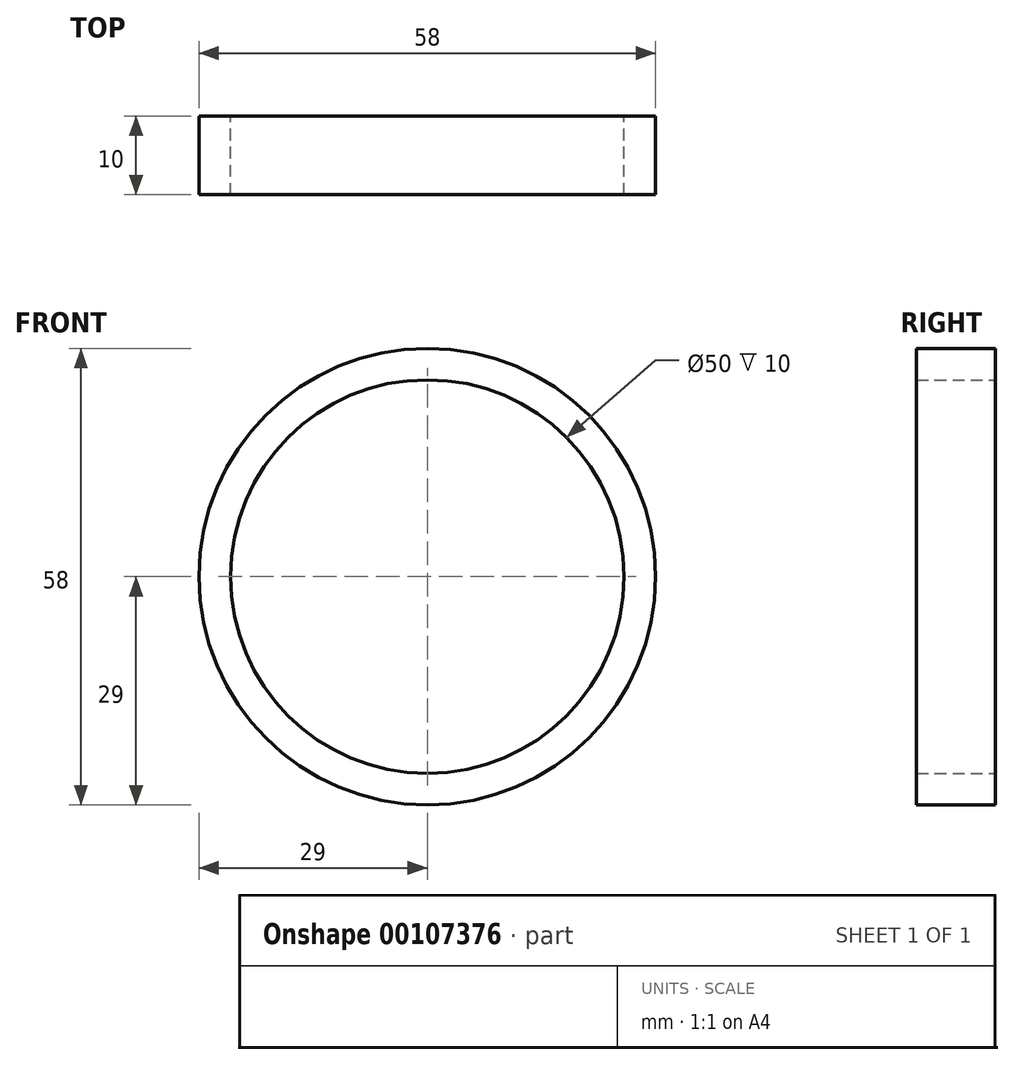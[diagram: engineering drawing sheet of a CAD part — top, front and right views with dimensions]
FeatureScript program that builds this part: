
annotation { "Feature Type Name" : "Feature", "Feature Type Description" : "" }
export const myFeature = defineFeature(function(context is Context, id is Id, definition is map)
    precondition{}
    {
        {
            var Q0;
            Q0=qCreatedBy(makeId("Front.planeOp"),FACE);
            var sketch = newSketch(context, id + "F0", { "sketchPlane" : qUnion([Q0])});
            skCircle(sketch, "E0", {"center": v(0, 0) * mm, "radius": 29 * mm});
            skSolve(sketch);
        }
        {
            var Q0;
            Q0=makeQuery(id+"F0.imprint","IMPRINT",FACE,{"disambiguationData":[TD([[makeQuery(id+"F0.imprint","IMPRINT",EDGE,{"derivedFrom":sQuery(id+"F0.wireOp",EDGE,"E0")}),1.0]])]});
            var sketch = newSketch(context, id + "F1", { "sketchPlane" : qUnion([Q0])});
            skCircle(sketch, "E1", {"center": v(0, 0) * mm, "radius": 25 * mm});
            skSolve(sketch);
        }
        {
            var Q0;
            Q0=makeQuery(id+"F0.imprint","IMPRINT",FACE,{"disambiguationData":[TD([[makeQuery(id+"F0.imprint","IMPRINT",EDGE,{"derivedFrom":sQuery(id+"F0.wireOp",EDGE,"E0")}),1.0]])]});
            extrude(context, id + "F2", {"entities" : qUnion([Q0]), "depth" : 10 * mm});
        }
        {
            var Q0;
            Q0=makeQuery(id+"F1.imprint","IMPRINT",FACE,{"disambiguationData":[TD([[makeQuery(id+"F1.imprint","IMPRINT",EDGE,{"derivedFrom":sQuery(id+"F1.wireOp",EDGE,"E1")}),1.0]])]});
            var sketch = newSketch(context, id + "F3", { "sketchPlane" : qUnion([Q0])});
            skPoint(sketch, "E2", {"position": v(0, 0) * mm});
            skSolve(sketch);
        }
        {
            var Q0;
            Q0=sQuery(id+"F3.wireOp",VERTEX,"E2");
            var Q1;
            Q1=makeQuery(id+"F2.opExtrude","SWEPT_BODY",BODY,{"disambiguationData":[OSD([sQuery(id+"F0.wireOp",EDGE,"E0")])]});
            hole(context, id + "F4", {"style" : HoleStyle.SIMPLE, "endStyle" : HoleEndStyle.BLIND, "oppositeDirection" : true, "holeDiameter" : 50 * mm, "holeDepth" : 10 * mm, "locations" : qUnion([Q0]), "scope" : qUnion([Q1])});
        }
    });
